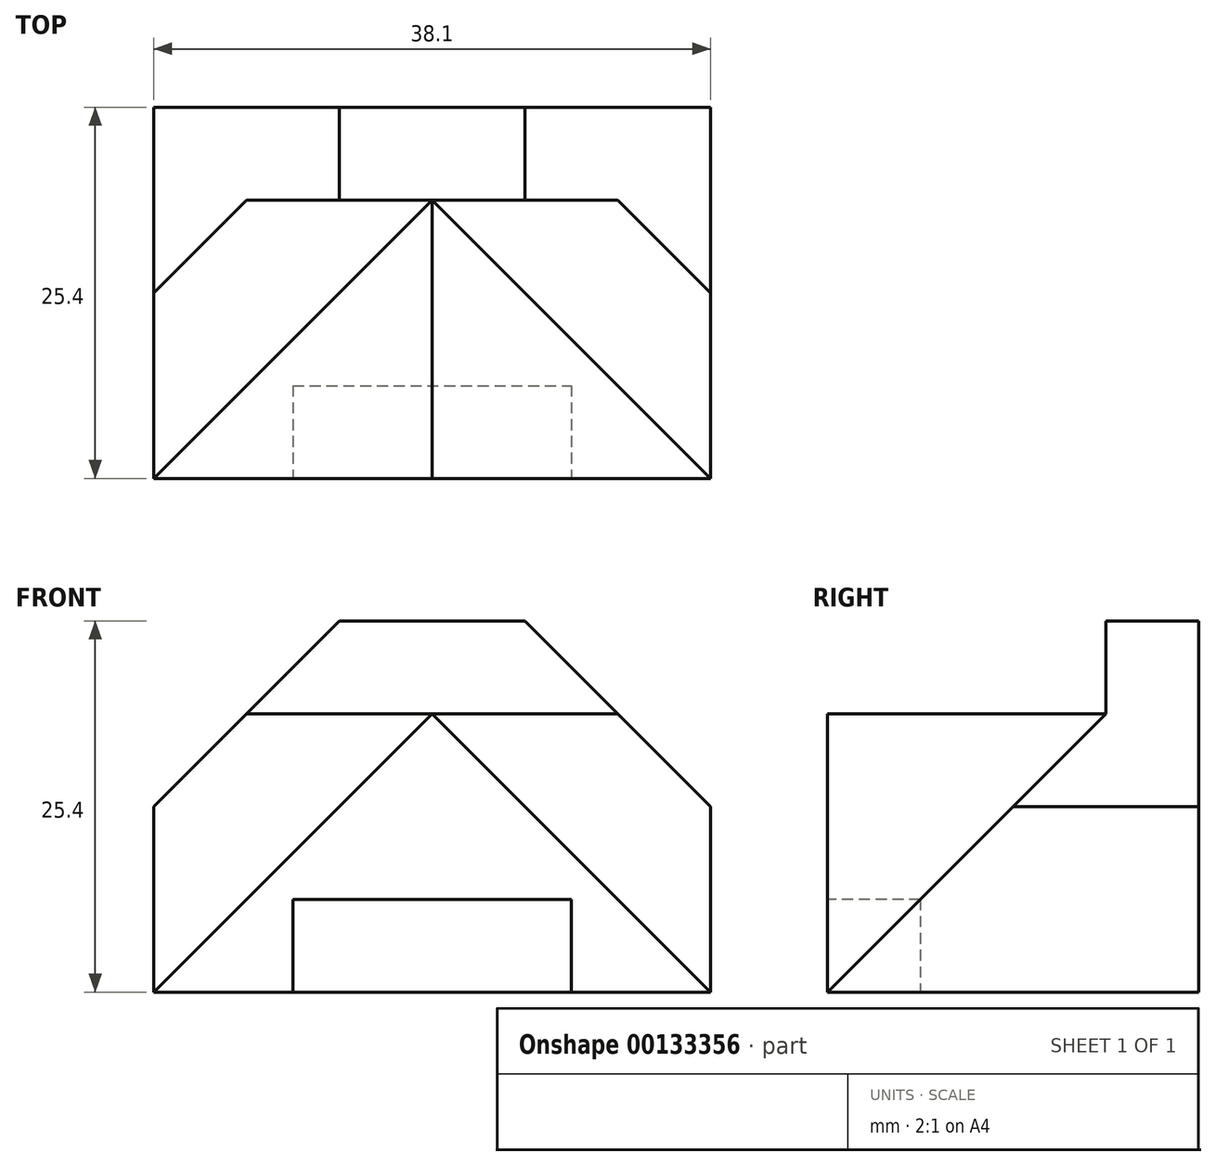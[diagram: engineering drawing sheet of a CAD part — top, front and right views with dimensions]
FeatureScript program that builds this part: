
annotation { "Feature Type Name" : "Feature", "Feature Type Description" : "" }
export const myFeature = defineFeature(function(context is Context, id is Id, definition is map)
    precondition{}
    {
        {
            var Q0;
            Q0=qCreatedBy(makeId("Top.planeOp"),FACE);
            var sketch = newSketch(context, id + "F0", { "sketchPlane" : qUnion([Q0])});
            skLineSegment(sketch, "E0.top", {"start": v(0, 25.4) * mm, "end": v(38.1, 25.4) * mm});
            skLineSegment(sketch, "E0.left", {"start": v(0, 0) * mm, "end": v(0, 25.4) * mm});
            skLineSegment(sketch, "E0.right", {"start": v(38.1, 0) * mm, "end": v(38.1, 25.4) * mm});
            skLineSegment(sketch, "E1", {"start": v(0, 19.05) * mm, "end": v(38.1, 19.05) * mm});
            skLineSegment(sketch, "E2", {"start": v(0, 0) * mm, "end": v(19.05, 19.05) * mm});
            skLineSegment(sketch, "E3", {"start": v(19.05, 19.05) * mm, "end": v(38.1, 0) * mm});
            skLineSegment(sketch, "E4", {"start": v(0, 0) * mm, "end": v(9.53, 0) * mm});
            skLineSegment(sketch, "E5", {"start": v(9.53, 0) * mm, "end": v(9.53, 6.35) * mm});
            skLineSegment(sketch, "E6", {"start": v(9.53, 6.35) * mm, "end": v(28.58, 6.35) * mm});
            skLineSegment(sketch, "E7", {"start": v(28.58, 6.35) * mm, "end": v(28.58, 0) * mm});
            skLineSegment(sketch, "E8", {"start": v(28.58, 0) * mm, "end": v(38.1, 0) * mm});
            skLineSegment(sketch, "E9", {"start": v(12.7, 25.4) * mm, "end": v(12.7, 19.05) * mm});
            skLineSegment(sketch, "E10", {"start": v(25.4, 25.4) * mm, "end": v(25.4, 19.05) * mm});
            skSolve(sketch);
        }
        {
            var Q0;
            {var subQ3=sQuery(id+"F0.wireOp",EDGE,"E9");Q0=makeQuery(id+"F0.imprint","IMPRINT",FACE,{"disambiguationData":[TD([[makeQuery(id+"F0.imprint","IMPRINT",EDGE,{"derivedFrom":subQ3}),1.0]])]});}
            var Q1;
            {var subQ3=sQuery(id+"F0.wireOp",EDGE,"E9");Q1=makeQuery(id+"F0.imprint","IMPRINT",FACE,{"disambiguationData":[TD([[makeQuery(id+"F0.imprint","IMPRINT",EDGE,{"derivedFrom":subQ3}),-1.0]])]});}
            var Q2;
            {var subQ3=sQuery(id+"F0.wireOp",EDGE,"E10");Q2=makeQuery(id+"F0.imprint","IMPRINT",FACE,{"disambiguationData":[TD([[makeQuery(id+"F0.imprint","IMPRINT",EDGE,{"derivedFrom":subQ3}),1.0]])]});}
            extrude(context, id + "F1", {"entities" : qUnion([Q0, Q1, Q2]), "depth" : 25.4 * mm});
        }
        {
            var Q0;
            Q0=makeQuery(id+"F1.opExtrude","SWEPT_FACE",FACE,{"disambiguationData":[OSD([sQuery(id+"F0.wireOp",EDGE,"E1")])]});
            var sketch = newSketch(context, id + "F2", { "sketchPlane" : qUnion([Q0])});
            skLineSegment(sketch, "E11.bottom", {"start": v(0, 25.4) * mm, "end": v(38.1, 25.4) * mm});
            skLineSegment(sketch, "E11.top", {"start": v(0, 0) * mm, "end": v(38.1, 0) * mm});
            skLineSegment(sketch, "E11.left", {"start": v(0, 25.4) * mm, "end": v(0, 0) * mm});
            skLineSegment(sketch, "E11.right", {"start": v(38.1, 25.4) * mm, "end": v(38.1, 0) * mm});
            skLineSegment(sketch, "E12", {"start": v(12.7, 25.4) * mm, "end": v(0, 12.7) * mm});
            skLineSegment(sketch, "E13", {"start": v(38.1, 12.7) * mm, "end": v(25.4, 25.4) * mm});
            skSolve(sketch);
        }
        {
            var Q0;
            {var subQ3=sQuery(id+"F2.wireOp",EDGE,"E12");Q0=makeQuery(id+"F2.imprint","IMPRINT",FACE,{"disambiguationData":[TD([[makeQuery(id+"F2.imprint","IMPRINT",EDGE,{"derivedFrom":subQ3}),-1.0]])]});}
            var Q1;
            {var subQ3=sQuery(id+"F2.wireOp",EDGE,"E13");Q1=makeQuery(id+"F2.imprint","IMPRINT",FACE,{"disambiguationData":[TD([[makeQuery(id+"F2.imprint","IMPRINT",EDGE,{"derivedFrom":subQ3}),-1.0]])]});}
            extrude(context, id + "F3", {"entities" : qUnion([Q0, Q1]), "operationType" : NewBodyOperationType.REMOVE, "endBound" : BoundingType.THROUGH_ALL, "oppositeDirection" : true, "depth" : 25.4 * mm});
        }
        {
            var Q0;
            Q0=makeQuery(id+"F0.imprint","IMPRINT",FACE,{"disambiguationData":[TD([[makeQuery(id+"F0.imprint","IMPRINT",EDGE,{"derivedFrom":sQuery(id+"F0.wireOp",EDGE,"E2")}),-1.0]])]});
            extrude(context, id + "F4", {"entities" : qUnion([Q0]), "depth" : 19.05 * mm});
        }
        {
            var Q0;
            Q0=makeQuery(id+"F4.opExtrude","SWEPT_FACE",FACE,{"disambiguationData":[OSD([sQuery(id+"F0.wireOp",EDGE,"E8")])]});
            var sketch = newSketch(context, id + "F5", { "sketchPlane" : qUnion([Q0])});
            skLineSegment(sketch, "E14.bottom", {"start": v(0, 0) * mm, "end": v(38.1, 0) * mm});
            skLineSegment(sketch, "E14.top", {"start": v(0, 19.05) * mm, "end": v(38.1, 19.05) * mm});
            skLineSegment(sketch, "E14.left", {"start": v(0, 0) * mm, "end": v(0, 19.05) * mm});
            skLineSegment(sketch, "E14.right", {"start": v(38.1, 0) * mm, "end": v(38.1, 19.05) * mm});
            skLineSegment(sketch, "E15", {"start": v(19.05, 19.05) * mm, "end": v(38.1, 0) * mm});
            skLineSegment(sketch, "E16", {"start": v(19.05, 19.05) * mm, "end": v(0, 0) * mm});
            skLineSegment(sketch, "E17.bottom", {"start": v(28.57, 6.35) * mm, "end": v(9.52, 6.35) * mm});
            skLineSegment(sketch, "E17.top", {"start": v(28.58, 0) * mm, "end": v(9.53, 0) * mm});
            skLineSegment(sketch, "E17.left", {"start": v(28.58, 6.35) * mm, "end": v(28.58, 0) * mm});
            skLineSegment(sketch, "E17.right", {"start": v(9.52, 6.35) * mm, "end": v(9.53, 0) * mm});
            skSolve(sketch);
        }
        {
            var Q0;
            {var subQ0=sQuery(id+"F5.wireOp",EDGE,"E14.right");Q0=makeQuery(id+"F5.imprint","IMPRINT",FACE,{"disambiguationData":[TD([[makeQuery(id+"F5.imprint","IMPRINT",EDGE,{"derivedFrom":subQ0}),-1.0]])]});}
            var Q1;
            {var subQ0=sQuery(id+"F5.wireOp",EDGE,"E14.top");var subQ1=makeQuery(id+"F4.opExtrude","SWEPT_EDGE",EDGE,{"disambiguationData":[OSD([sQuery(id+"F0.wireOp",EDGE,"E7"),sQuery(id+"F0.wireOp",EDGE,"E8")])]});var subQ2=makeQuery(id+"F5.imprint","INTERSECT",VERTEX,{"derivedFrom":[subQ1,subQ0]});Q1=makeQuery(id+"F5.imprint","IMPRINT",FACE,{"disambiguationData":[TD([[makeQuery(id+"F5.imprint","IMPRINT",EDGE,{"disambiguationData":[TD([[subQ2,1.0]])],"derivedFrom":subQ0}),-1.0]])]});}
            var Q2;
            {var subQ0=sQuery(id+"F5.wireOp",EDGE,"E14.left");Q2=makeQuery(id+"F5.imprint","IMPRINT",FACE,{"disambiguationData":[TD([[makeQuery(id+"F5.imprint","IMPRINT",EDGE,{"derivedFrom":subQ0}),-1.0]])]});}
            extrude(context, id + "F6", {"entities" : qUnion([Q0, Q1, Q2]), "operationType" : NewBodyOperationType.REMOVE, "oppositeDirection" : true, "depth" : 19.05 * mm});
        }
        {
            var Q0;
            {var subQ0=sQuery(id+"F0.wireOp",EDGE,"E3");Q0=makeQuery(id+"F0.imprint","IMPRINT",FACE,{"disambiguationData":[TD([[makeQuery(id+"F0.imprint","IMPRINT",EDGE,{"derivedFrom":subQ0}),1.0]])]});}
            var Q1;
            {var subQ0=sQuery(id+"F0.wireOp",EDGE,"E2");Q1=makeQuery(id+"F0.imprint","IMPRINT",FACE,{"disambiguationData":[TD([[makeQuery(id+"F0.imprint","IMPRINT",EDGE,{"derivedFrom":subQ0}),1.0]])]});}
            extrude(context, id + "F7", {"entities" : qUnion([Q0, Q1]), "operationType" : NewBodyOperationType.ADD, "depth" : 25.4 * mm});
        }
        {
            var Q0;
            {var subQ0=sQuery(id+"F0.wireOp",EDGE,"E0.right");Q0=makeQuery(id+"F7.boolean.opBoolean","MERGE",FACE,{"derivedFrom":[makeQuery(id+"F1.opExtrude","SWEPT_FACE",FACE,{"disambiguationData":[OSD([subQ0])]}),makeQuery(id+"F7.opExtrude","SWEPT_FACE",FACE,{"disambiguationData":[OSD([subQ0])]})]});}
            var sketch = newSketch(context, id + "F8", { "sketchPlane" : qUnion([Q0])});
            skLineSegment(sketch, "E18", {"start": v(19.05, 19.05) * mm, "end": v(0, 0) * mm});
            skLineSegment(sketch, "E19.bottom", {"start": v(19.05, 12.7) * mm, "end": v(25.4, 12.7) * mm});
            skLineSegment(sketch, "E19.top", {"start": v(19.05, 25.4) * mm, "end": v(25.4, 25.4) * mm});
            skLineSegment(sketch, "E19.left", {"start": v(19.05, 12.7) * mm, "end": v(19.05, 25.4) * mm});
            skLineSegment(sketch, "E19.right", {"start": v(25.4, 12.7) * mm, "end": v(25.4, 25.4) * mm});
            skLineSegment(sketch, "E20", {"start": v(19.05, 25.4) * mm, "end": v(0, 25.4) * mm});
            skLineSegment(sketch, "E21", {"start": v(0, 25.4) * mm, "end": v(0, 0) * mm});
            skLineSegment(sketch, "E22", {"start": v(25.4, 0) * mm, "end": v(25.4, 12.7) * mm});
            skLineSegment(sketch, "E23", {"start": v(25.4, 0) * mm, "end": v(0, 0) * mm});
            skLineSegment(sketch, "E24", {"start": v(0, 0) * mm, "end": v(0, 25.4) * mm});
            skSolve(sketch);
        }
        {
            var Q0;
            {var subQ0=sQuery(id+"F8.wireOp",EDGE,"E18");Q0=makeQuery(id+"F8.imprint","IMPRINT",FACE,{"disambiguationData":[TD([[makeQuery(id+"F8.imprint","IMPRINT",EDGE,{"derivedFrom":subQ0}),-1.0]])]});}
            extrude(context, id + "F9", {"entities" : qUnion([Q0]), "operationType" : NewBodyOperationType.REMOVE, "endBound" : BoundingType.THROUGH_ALL, "oppositeDirection" : true, "depth" : 25.4 * mm});
        }
        {
            var Q0;
            {var subQ0=sQuery(id+"F5.wireOp",EDGE,"E16");Q0=makeQuery(id+"F5.imprint","IMPRINT",FACE,{"disambiguationData":[TD([[makeQuery(id+"F5.imprint","IMPRINT",EDGE,{"derivedFrom":subQ0}),1.0]])]});}
            var Q1;
            {var subQ3=sQuery(id+"F5.wireOp",EDGE,"E17.left");Q1=makeQuery(id+"F5.imprint","IMPRINT",FACE,{"disambiguationData":[TD([[makeQuery(id+"F5.imprint","IMPRINT",EDGE,{"derivedFrom":subQ3}),1.0]])]});}
            extrude(context, id + "F10", {"entities" : qUnion([Q0, Q1]), "operationType" : NewBodyOperationType.ADD, "oppositeDirection" : true, "depth" : 25.4 * mm});
        }
        {
            var Q0;
            {var subQ0=sQuery(id+"F5.wireOp",EDGE,"E14.right");Q0=makeQuery(id+"F5.imprint","IMPRINT",FACE,{"disambiguationData":[TD([[makeQuery(id+"F5.imprint","IMPRINT",EDGE,{"derivedFrom":subQ0}),-1.0]])]});}
            var sketch = newSketch(context, id + "F11", { "sketchPlane" : qUnion([Q0])});
            skLineSegment(sketch, "E25", {"start": v(38.1, 19.05) * mm, "end": v(31.75, 19.05) * mm});
            skLineSegment(sketch, "E26", {"start": v(19.05, 19.05) * mm, "end": v(38.1, 0) * mm});
            skLineSegment(sketch, "E27", {"start": v(38.1, 12.7) * mm, "end": v(38.1, 19.05) * mm});
            skLineSegment(sketch, "E28", {"start": v(31.75, 19.05) * mm, "end": v(38.1, 12.7) * mm});
            skLineSegment(sketch, "E29", {"start": v(19.05, 19.05) * mm, "end": v(19.05, 0) * mm, "construction": true});
            skLineSegment(sketch, "E30.MirrorCS", {"start": v(0, 19.05) * mm, "end": v(6.35, 19.05) * mm});
            skLineSegment(sketch, "E31.MirrorCS", {"start": v(19.05, 19.05) * mm, "end": v(0, 0) * mm});
            skLineSegment(sketch, "E32.MirrorCS", {"start": v(6.35, 19.05) * mm, "end": v(0, 12.7) * mm});
            skLineSegment(sketch, "E33.MirrorCS", {"start": v(0, 12.7) * mm, "end": v(0, 19.05) * mm});
            skPoint(sketch, "E34.orphan", {"position": v(19.05, 19.05) * mm});
            skPoint(sketch, "E35.orphan", {"position": v(0, 0) * mm});
            skSolve(sketch);
        }
        {
            var Q0;
            Q0=makeQuery(id+"F11.imprint","IMPRINT",FACE,{"disambiguationData":[TD([[makeQuery(id+"F11.imprint","IMPRINT",EDGE,{"derivedFrom":sQuery(id+"F11.wireOp",EDGE,"E30.MirrorCS")}),-1.0]])]});
            var Q1;
            Q1=makeQuery(id+"F11.imprint","IMPRINT",FACE,{"disambiguationData":[TD([[makeQuery(id+"F11.imprint","IMPRINT",EDGE,{"derivedFrom":sQuery(id+"F11.wireOp",EDGE,"E25")}),-1.0]])]});
            extrude(context, id + "F12", {"entities" : qUnion([Q0, Q1]), "operationType" : NewBodyOperationType.REMOVE, "endBound" : BoundingType.THROUGH_ALL, "oppositeDirection" : true, "depth" : 25.4 * mm});
        }
    });
